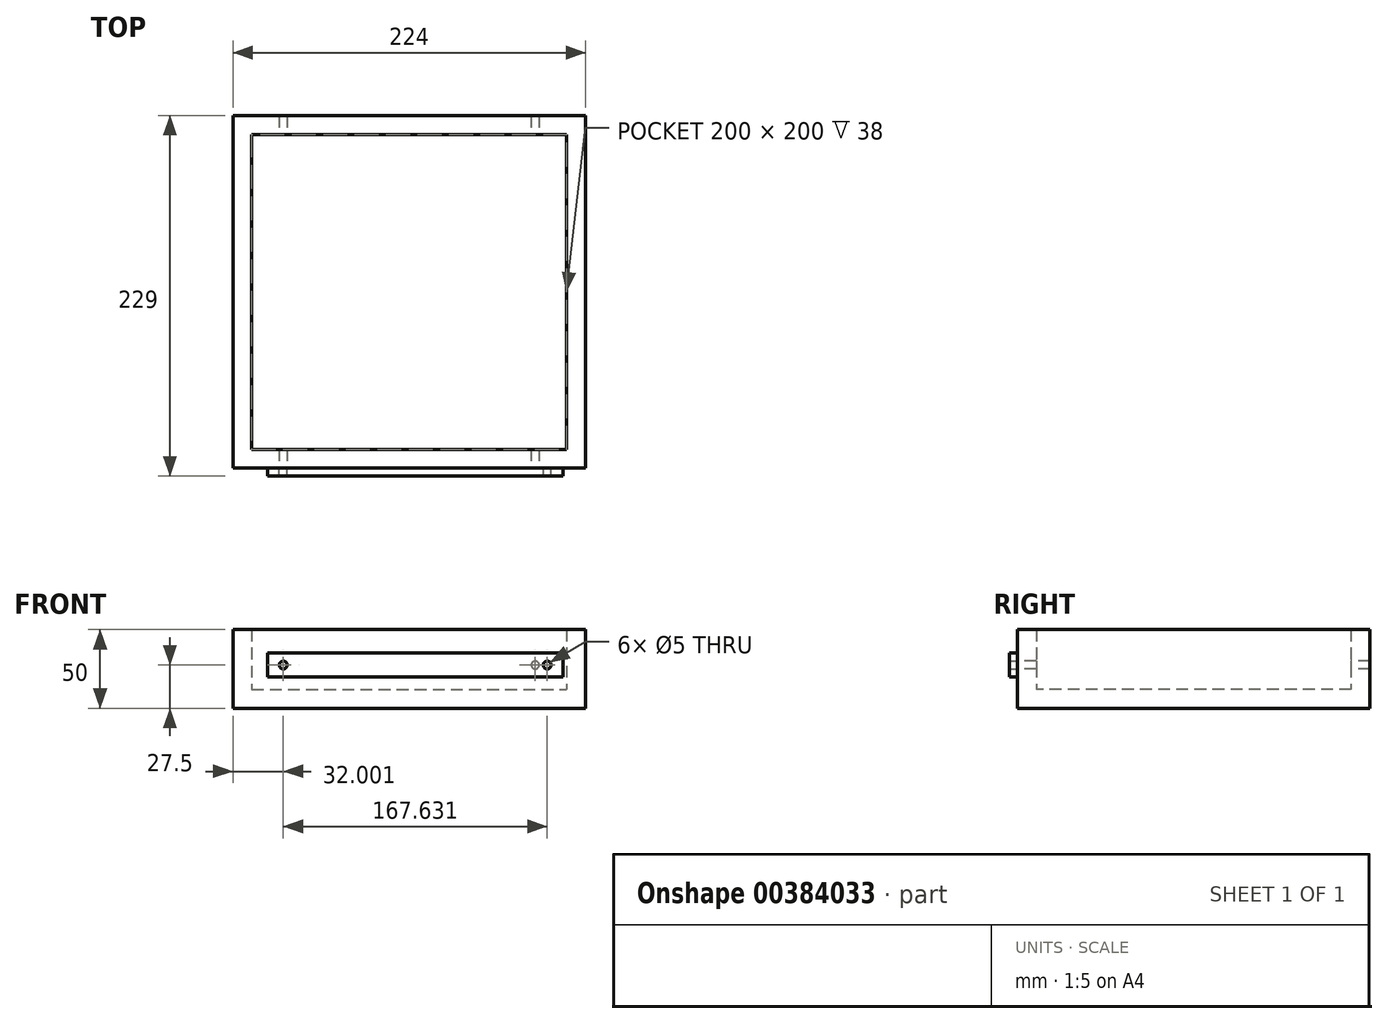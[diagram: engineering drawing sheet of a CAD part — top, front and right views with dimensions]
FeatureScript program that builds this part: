
annotation { "Feature Type Name" : "Feature", "Feature Type Description" : "" }
export const myFeature = defineFeature(function(context is Context, id is Id, definition is map)
    precondition{}
    {
        {
            var Q0;
            Q0=qCreatedBy(makeId("Top.planeOp"),FACE);
            var sketch = newSketch(context, id + "F0", { "sketchPlane" : qUnion([Q0])});
            skLineSegment(sketch, "E0.bottom", {"start": v(-209.15, 171) * mm, "end": v(-9.15, 171) * mm});
            skLineSegment(sketch, "E0.top", {"start": v(-209.15, -29) * mm, "end": v(-9.15, -29) * mm});
            skLineSegment(sketch, "E0.left", {"start": v(-209.15, 171) * mm, "end": v(-209.15, -29) * mm});
            skLineSegment(sketch, "E0.right", {"start": v(-9.15, 171) * mm, "end": v(-9.15, -29) * mm});
            skLineSegment(sketch, "E1.0", {"start": v(-221.15, -41) * mm, "end": v(2.85, -41) * mm});
            skLineSegment(sketch, "E1.1", {"start": v(-221.15, 183) * mm, "end": v(-221.15, -41) * mm});
            skLineSegment(sketch, "E1.2", {"start": v(-221.15, 183) * mm, "end": v(2.85, 183) * mm});
            skLineSegment(sketch, "E1.3", {"start": v(2.85, 183) * mm, "end": v(2.85, -41) * mm});
            skSolve(sketch);
        }
        {
            var Q0;
            Q0 = qSketchRegion(id + "F0", true);
            extrude(context, id + "F1", {"entities" : qUnion([Q0]), "depth" : 50 * mm});
        }
        {
            var Q0;
            Q0=makeQuery(id+"F0.imprint","IMPRINT",FACE,{"disambiguationData":[TD([[makeQuery(id+"F0.imprint","IMPRINT",EDGE,{"derivedFrom":sQuery(id+"F0.wireOp",EDGE,"E0.bottom")}),-1.0]])]});
            extrude(context, id + "F2", {"entities" : qUnion([Q0]), "operationType" : NewBodyOperationType.ADD, "depth" : 12 * mm});
        }
        {
            var Q0;
            Q0=makeQuery(id+"F1.opExtrude","SWEPT_FACE",FACE,{"disambiguationData":[OSD([sQuery(id+"F0.wireOp",EDGE,"E1.0")])]});
            var sketch = newSketch(context, id + "F3", { "sketchPlane" : qUnion([Q0])});
            skCircle(sketch, "E2", {"center": v(-189.15, 27.5) * mm, "radius": 2.5 * mm});
            skCircle(sketch, "E3", {"center": v(-21.52, 27.5) * mm, "radius": 2.5 * mm});
            skLineSegment(sketch, "E4.bottom", {"start": v(-199.15, 35) * mm, "end": v(-11.52, 35) * mm});
            skLineSegment(sketch, "E4.top", {"start": v(-199.15, 20) * mm, "end": v(-11.52, 20) * mm});
            skLineSegment(sketch, "E4.left", {"start": v(-199.15, 35) * mm, "end": v(-199.15, 20) * mm});
            skLineSegment(sketch, "E4.right", {"start": v(-11.52, 35) * mm, "end": v(-11.52, 20) * mm});
            skLineSegment(sketch, "E5.bottom", {"start": v(-221.15, 0) * mm, "end": v(2.85, 0) * mm});
            skLineSegment(sketch, "E5.top", {"start": v(-221.15, -50) * mm, "end": v(2.85, -50) * mm});
            skLineSegment(sketch, "E5.left", {"start": v(-221.15, 0) * mm, "end": v(-221.15, -50) * mm});
            skLineSegment(sketch, "E5.right", {"start": v(2.85, 0) * mm, "end": v(2.85, -50) * mm});
            skCircle(sketch, "E6", {"center": v(-189.15, -22.5) * mm, "radius": 2.5 * mm});
            skCircle(sketch, "E7", {"center": v(-29.15, -22.5) * mm, "radius": 2.5 * mm});
            skLineSegment(sketch, "E8.bottom", {"start": v(-199.15, -15) * mm, "end": v(-19.15, -15) * mm});
            skLineSegment(sketch, "E8.top", {"start": v(-199.15, -30) * mm, "end": v(-19.15, -30) * mm});
            skLineSegment(sketch, "E8.left", {"start": v(-199.15, -15) * mm, "end": v(-199.15, -30) * mm});
            skLineSegment(sketch, "E8.right", {"start": v(-19.15, -15) * mm, "end": v(-19.15, -30) * mm});
            skLineSegment(sketch, "E9", {"start": v(-189.15, 27.5) * mm, "end": v(-29.15, -22.5) * mm});
            skCircle(sketch, "E10", {"center": v(-29.15, 27.5) * mm, "radius": 2.5 * mm});
            skSolve(sketch);
        }
        {
            var Q0;
            Q0=makeQuery(id+"F3.imprint","IMPRINT",FACE,{"disambiguationData":[TD([[makeQuery(id+"F3.imprint","IMPRINT",EDGE,{"derivedFrom":sQuery(id+"F3.wireOp",EDGE,"E2")}),-1.0]])]});
            var Q1;
            Q1=makeQuery(id+"F3.imprint","IMPRINT",FACE,{"disambiguationData":[TD([[makeQuery(id+"F3.imprint","IMPRINT",EDGE,{"derivedFrom":sQuery(id+"F3.wireOp",EDGE,"E10")}),1.0]])]});
            extrude(context, id + "F4", {"entities" : qUnion([Q0, Q1]), "depth" : 5 * mm});
        }
        {
            var Q0;
            Q0=makeQuery(id+"F3.imprint","IMPRINT",FACE,{"disambiguationData":[TD([[makeQuery(id+"F3.imprint","IMPRINT",EDGE,{"derivedFrom":sQuery(id+"F3.wireOp",EDGE,"E10")}),1.0]])]});
            var Q1;
            Q1=makeQuery(id+"F3.imprint","IMPRINT",FACE,{"disambiguationData":[TD([[makeQuery(id+"F3.imprint","IMPRINT",EDGE,{"derivedFrom":sQuery(id+"F3.wireOp",EDGE,"E2")}),1.0]])]});
            extrude(context, id + "F5", {"entities" : qUnion([Q0, Q1]), "operationType" : NewBodyOperationType.REMOVE, "oppositeDirection" : true, "depth" : 300 * mm});
        }
    });
